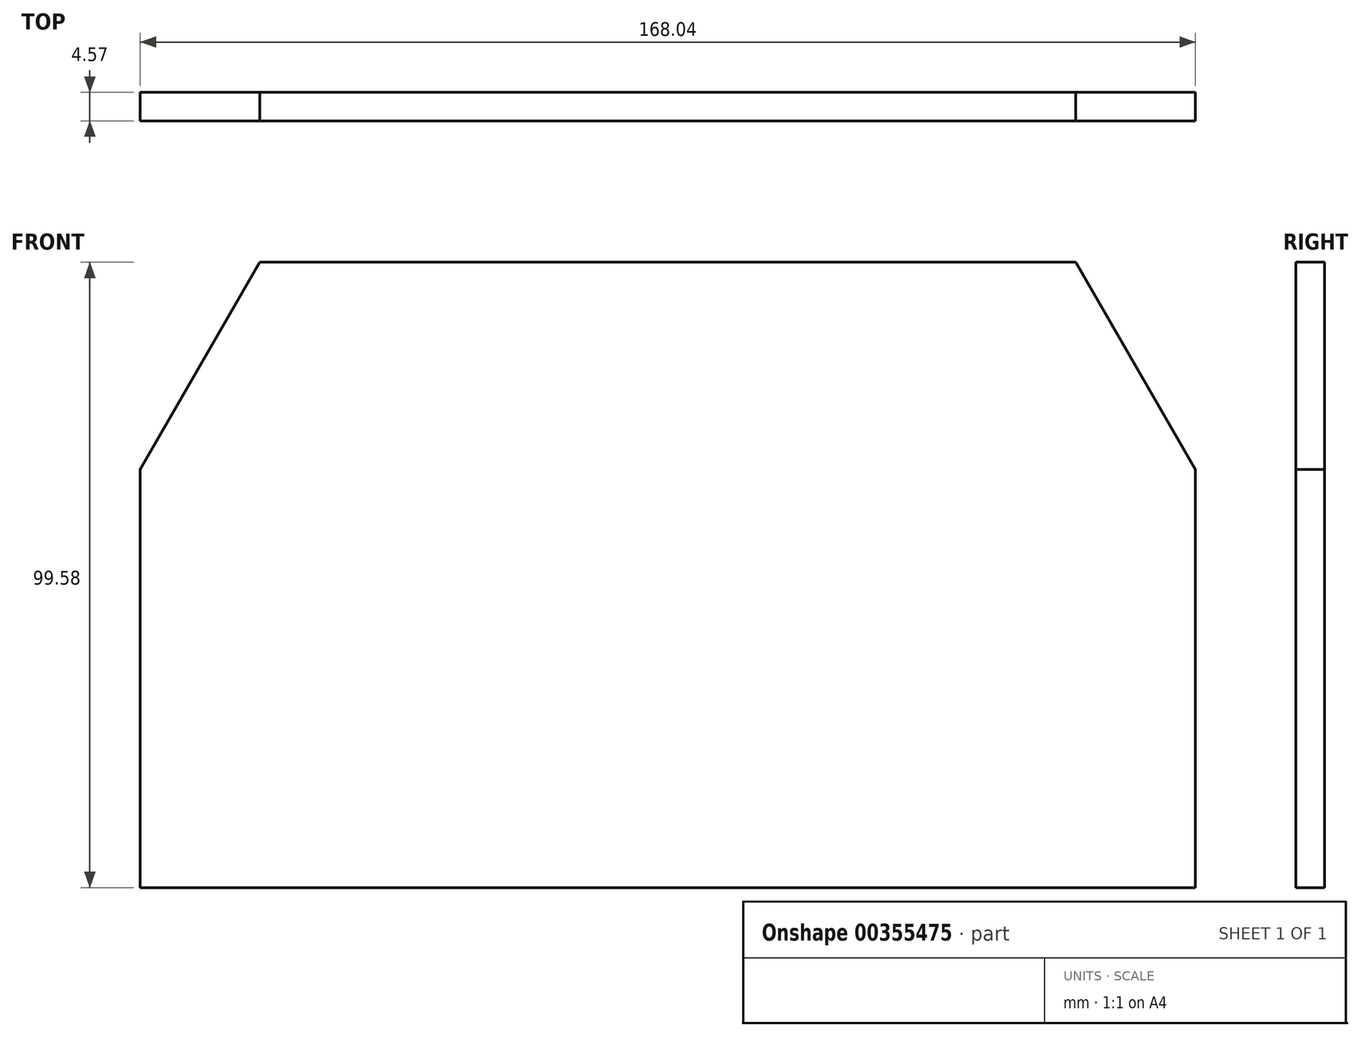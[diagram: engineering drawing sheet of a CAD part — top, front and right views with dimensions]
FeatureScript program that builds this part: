
annotation { "Feature Type Name" : "Feature", "Feature Type Description" : "" }
export const myFeature = defineFeature(function(context is Context, id is Id, definition is map)
    precondition{}
    {
        {
            var Q0;
            Q0=qCreatedBy(makeId("Front.planeOp"),FACE);
            var sketch = newSketch(context, id + "F0", { "sketchPlane" : qUnion([Q0])});
            skLineSegment(sketch, "E0.bottom", {"start": v(-84.02, 73.44) * mm, "end": v(84.02, 73.44) * mm});
            skLineSegment(sketch, "E0.top", {"start": v(-84.02, -26.14) * mm, "end": v(84.02, -26.14) * mm});
            skLineSegment(sketch, "E0.left", {"start": v(-84.02, 73.44) * mm, "end": v(-84.02, -26.14) * mm});
            skLineSegment(sketch, "E0.right", {"start": v(84.02, 73.44) * mm, "end": v(84.02, -26.14) * mm});
            skPoint(sketch, "E0.middle", {"position": v(0, 23.65) * mm});
            skSolve(sketch);
        }
        {
            var Q0;
            Q0=makeQuery(id+"F0.imprint","IMPRINT",FACE,{"disambiguationData":[TD([[makeQuery(id+"F0.imprint","IMPRINT",EDGE,{"derivedFrom":sQuery(id+"F0.wireOp",EDGE,"E0.bottom")}),-1.0]])]});
            extrude(context, id + "F1", {"entities" : qUnion([Q0]), "depth" : 4.57 * mm});
        }
        {
            var Q0;
            Q0=makeQuery(id+"F1.opExtrude","SWEPT_EDGE",EDGE,{"disambiguationData":[OSD([sQuery(id+"F0.wireOp",EDGE,"E0.bottom"),sQuery(id+"F0.wireOp",EDGE,"E0.left")])]});
            var Q1;
            Q1=makeQuery(id+"F1.opExtrude","SWEPT_EDGE",EDGE,{"disambiguationData":[OSD([sQuery(id+"F0.wireOp",EDGE,"E0.bottom"),sQuery(id+"F0.wireOp",EDGE,"E0.right")])]});
            chamfer(context, id + "F2", {"entities" : qUnion([Q0, Q1]), "chamferType" : ChamferType.OFFSET_ANGLE, "width" : 33.02 * mm, "oppositeDirection" : false, "angle" : 30 * degree, "tangentPropagation" : true});
        }
    });
